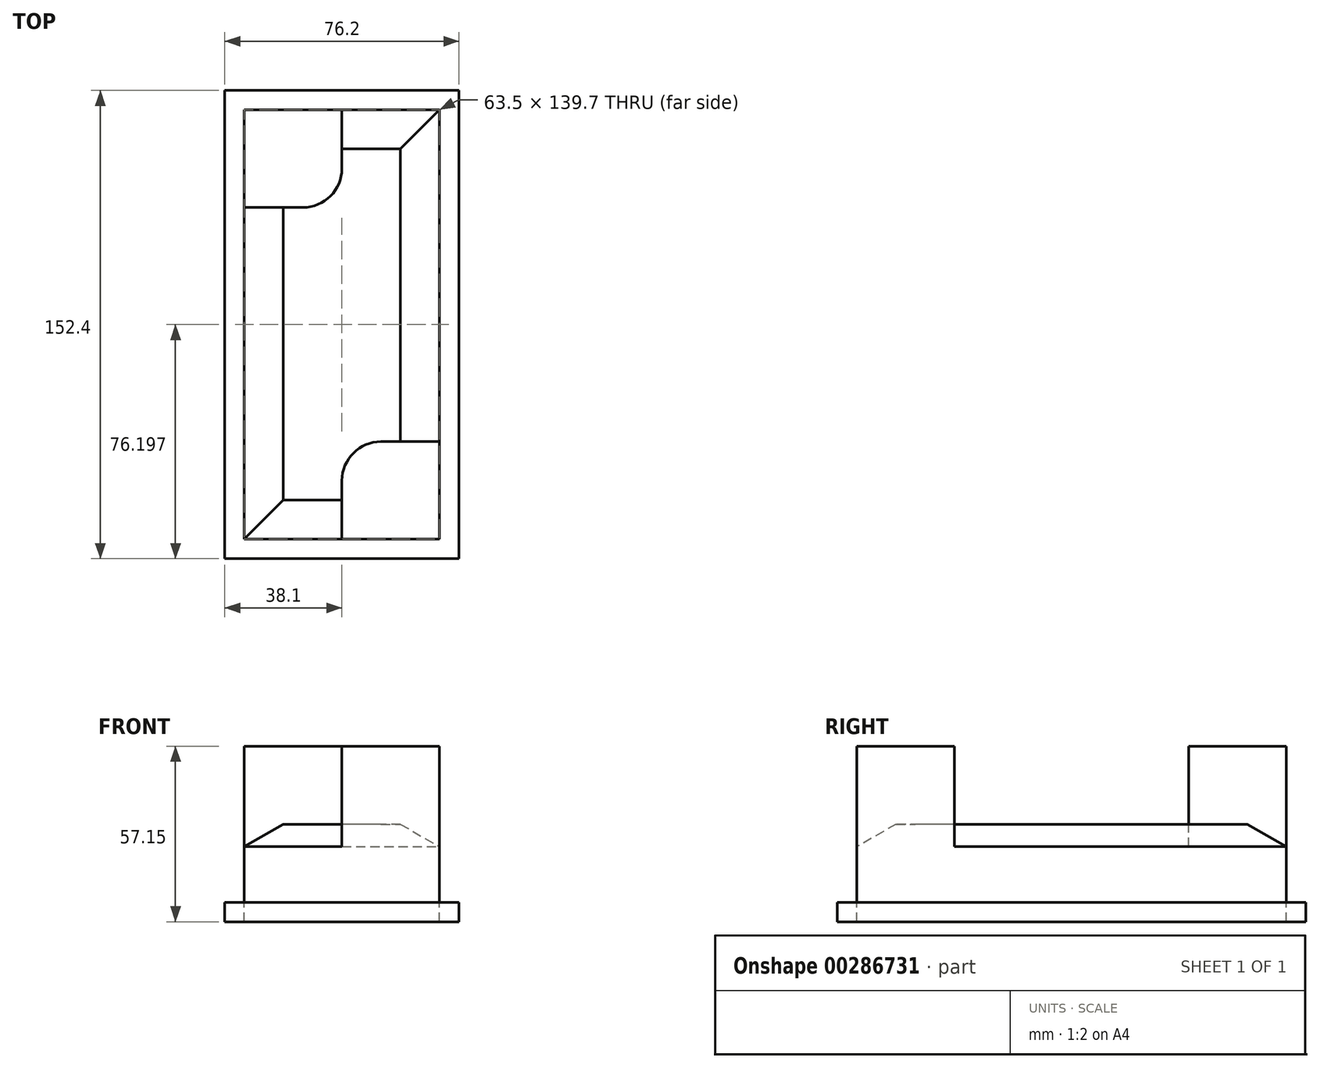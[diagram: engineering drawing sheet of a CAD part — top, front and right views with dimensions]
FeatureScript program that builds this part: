
annotation { "Feature Type Name" : "Feature", "Feature Type Description" : "" }
export const myFeature = defineFeature(function(context is Context, id is Id, definition is map)
    precondition{}
    {
        {
            var Q0;
            Q0=qCreatedBy(makeId("Top.planeOp"),FACE);
            var sketch = newSketch(context, id + "F0", { "sketchPlane" : qUnion([Q0])});
            skLineSegment(sketch, "E0.bottom", {"start": v(-38.1, 76.27) * mm, "end": v(38.1, 76.27) * mm});
            skLineSegment(sketch, "E0.top", {"start": v(-38.1, -76.13) * mm, "end": v(38.1, -76.13) * mm});
            skLineSegment(sketch, "E0.left", {"start": v(-38.1, 76.27) * mm, "end": v(-38.1, -76.13) * mm});
            skLineSegment(sketch, "E0.right", {"start": v(38.1, 76.27) * mm, "end": v(38.1, -76.13) * mm});
            skLineSegment(sketch, "E1.bottom", {"start": v(-31.75, 69.92) * mm, "end": v(31.75, 69.92) * mm});
            skLineSegment(sketch, "E1.top", {"start": v(-31.75, -69.78) * mm, "end": v(31.75, -69.78) * mm});
            skLineSegment(sketch, "E1.left", {"start": v(-31.75, 69.92) * mm, "end": v(-31.75, -69.78) * mm});
            skLineSegment(sketch, "E1.right", {"start": v(31.75, 69.92) * mm, "end": v(31.75, -69.78) * mm});
            skLineSegment(sketch, "E2", {"start": v(0, 69.92) * mm, "end": v(0, 50.87) * mm});
            skLineSegment(sketch, "E3", {"start": v(-12.7, 38.17) * mm, "end": v(-31.75, 38.17) * mm});
            skLineSegment(sketch, "E4", {"start": v(0, -69.78) * mm, "end": v(0, -50.73) * mm});
            skLineSegment(sketch, "E5", {"start": v(12.7, -38.03) * mm, "end": v(31.75, -38.03) * mm});
            skPoint(sketch, "E6.visualSharp", {"position": v(0, 38.17) * mm});
            skArc(sketch, "E6.filletArc", {"start": v(-12.7, 38.17) * mm, "mid": v(-3.72, 41.89) * mm, "end": v(0, 50.87) * mm});
            skPoint(sketch, "E7.visualSharp", {"position": v(0, -38.03) * mm});
            skArc(sketch, "E7.filletArc", {"start": v(12.7, -38.03) * mm, "mid": v(3.72, -41.75) * mm, "end": v(0, -50.73) * mm});
            skSolve(sketch);
        }
        {
            var Q0;
            Q0 = qSketchRegion(id + "F0", true);
            extrude(context, id + "F1", {"entities" : qUnion([Q0]), "oppositeDirection" : true, "depth" : 6.35 * mm});
        }
        {
            var Q0;
            {var subQ9=sQuery(id+"F0.wireOp",EDGE,"E2");Q0=makeQuery(id+"F0.imprint","IMPRINT",FACE,{"disambiguationData":[TD([[makeQuery(id+"F0.imprint","IMPRINT",EDGE,{"derivedFrom":subQ9}),1.0]])]});}
            extrude(context, id + "F2", {"entities" : qUnion([Q0]), "depth" : 25.4 * mm});
        }
        {
            var Q0;
            Q0=makeQuery(id+"F2.opExtrude","CAP_EDGE",EDGE,{"disambiguationData":[OSD([sQuery(id+"F0.wireOp",EDGE,"E1.top")])],"isStart":false});
            var Q1;
            Q1=makeQuery(id+"F2.opExtrude","CAP_EDGE",EDGE,{"disambiguationData":[OSD([sQuery(id+"F0.wireOp",EDGE,"E1.left")])],"isStart":false});
            var Q2;
            Q2=makeQuery(id+"F2.opExtrude","CAP_EDGE",EDGE,{"disambiguationData":[OSD([sQuery(id+"F0.wireOp",EDGE,"E1.right")])],"isStart":false});
            var Q3;
            Q3=makeQuery(id+"F2.opExtrude","CAP_EDGE",EDGE,{"disambiguationData":[OSD([sQuery(id+"F0.wireOp",EDGE,"E1.bottom")])],"isStart":false});
            chamfer(context, id + "F3", {"entities" : qUnion([Q0, Q1, Q2, Q3]), "chamferType" : ChamferType.OFFSET_ANGLE, "width" : 12.7 * mm, "oppositeDirection" : false, "angle" : 30 * degree, "tangentPropagation" : true});
        }
        {
            var Q0;
            {var subQ0=sQuery(id+"F0.wireOp",EDGE,"E2");Q0=makeQuery(id+"F0.imprint","IMPRINT",FACE,{"disambiguationData":[TD([[makeQuery(id+"F0.imprint","IMPRINT",EDGE,{"derivedFrom":subQ0}),-1.0]])]});}
            var Q1;
            {var subQ1=sQuery(id+"F0.wireOp",EDGE,"E4");Q1=makeQuery(id+"F0.imprint","IMPRINT",FACE,{"disambiguationData":[TD([[makeQuery(id+"F0.imprint","IMPRINT",EDGE,{"derivedFrom":subQ1}),-1.0]])]});}
            extrude(context, id + "F4", {"entities" : qUnion([Q0, Q1]), "operationType" : NewBodyOperationType.ADD, "depth" : 50.8 * mm});
        }
    });
